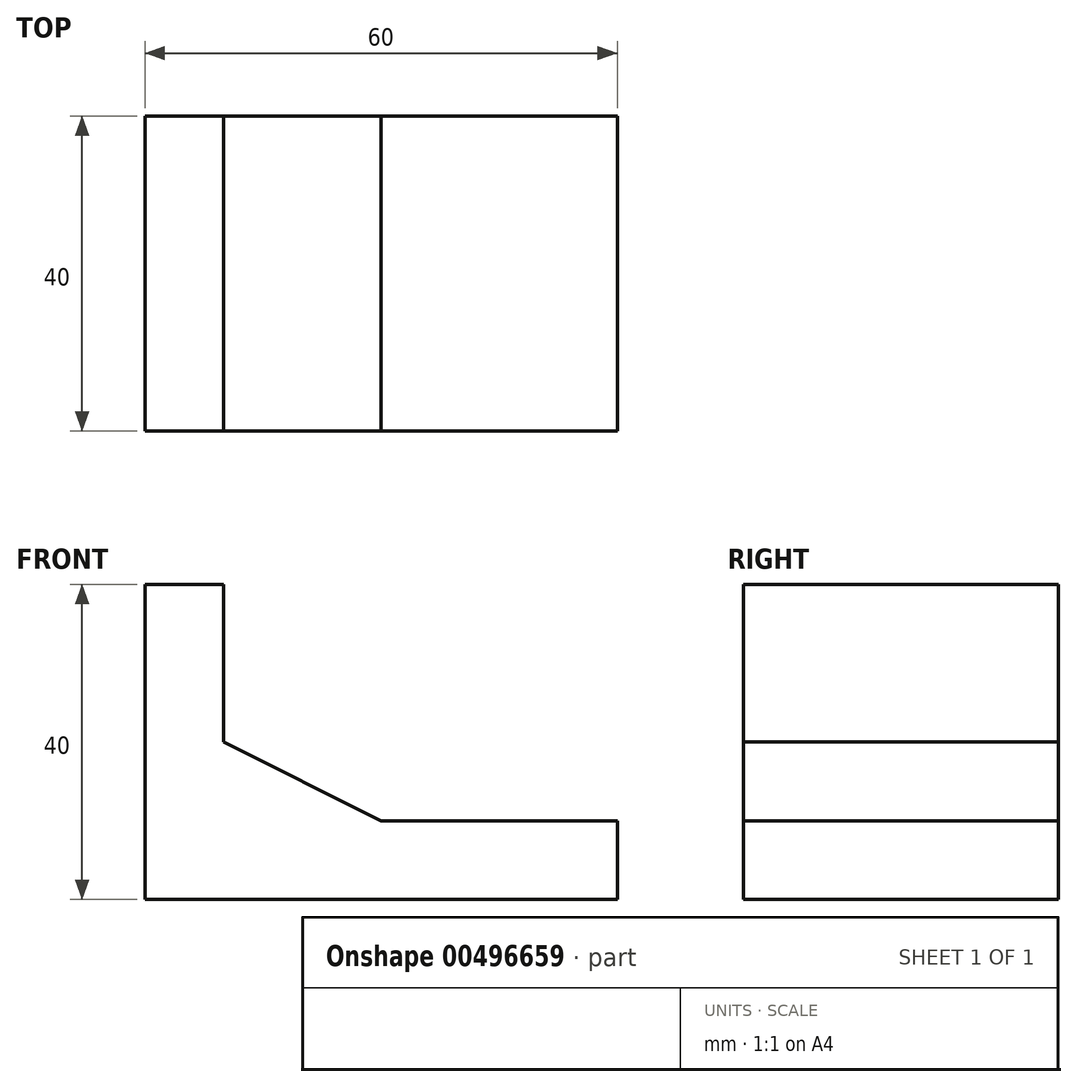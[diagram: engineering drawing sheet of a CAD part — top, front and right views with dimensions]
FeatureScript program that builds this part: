
annotation { "Feature Type Name" : "Feature", "Feature Type Description" : "" }
export const myFeature = defineFeature(function(context is Context, id is Id, definition is map)
    precondition{}
    {
        {
            var Q0;
            Q0=qCreatedBy(makeId("Front.planeOp"),FACE);
            var sketch = newSketch(context, id + "F0", { "sketchPlane" : qUnion([Q0])});
            skLineSegment(sketch, "E0", {"start": v(0, 0) * mm, "end": v(0, 40) * mm});
            skLineSegment(sketch, "E1", {"start": v(0, 40) * mm, "end": v(10, 40) * mm});
            skLineSegment(sketch, "E2", {"start": v(0, 0) * mm, "end": v(60, 0) * mm});
            skLineSegment(sketch, "E3", {"start": v(60, 0) * mm, "end": v(60, 10) * mm});
            skLineSegment(sketch, "E4", {"start": v(60, 10) * mm, "end": v(30, 10) * mm});
            skLineSegment(sketch, "E5", {"start": v(30, 10) * mm, "end": v(10, 20) * mm});
            skLineSegment(sketch, "E6", {"start": v(10, 20) * mm, "end": v(10, 40) * mm});
            skSolve(sketch);
        }
        {
            var Q0;
            Q0 = qSketchRegion(id + "F0", true);
            extrude(context, id + "F1", {"entities" : qUnion([Q0]), "depth" : 40 * mm});
        }
    });
